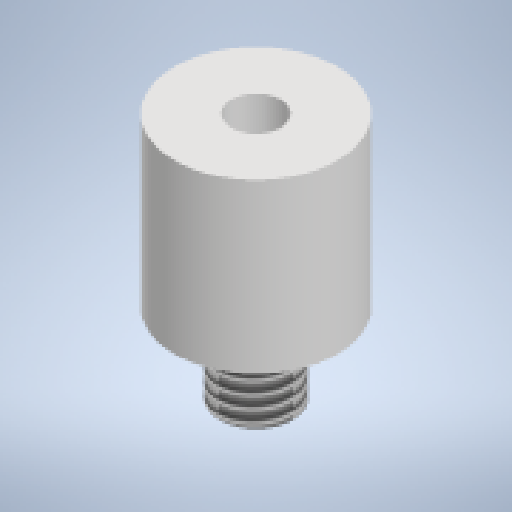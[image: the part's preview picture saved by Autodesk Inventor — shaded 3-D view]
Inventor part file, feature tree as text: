
AUTODESK INVENTOR PART (.ipt)
format: ipt  version: 2023 (Build 270158000, 158)  size: 164,864 bytes
history: native  units: mm
features: revolve x1, thread x1, sketch x1
ambient origin geometry x8: Origin, YZ Plane, XZ Plane, XY Plane, X Axis, Y Axis, Z Axis, Center Point
bodies: Solid1 (feature_tree)
feature tree (3):
  revolve  "Revolution1"  [1 undecoded]
  thread  "Thread1"  [1 undecoded]
  sketch  "Sketch1"  dims[d4=0.5mm d5=1.5mm d6=0.8mm d7=1.0mm d8=360.0deg d9=5.0mm d10=0.0mm d11=8.0mm d12=2.0mm d13=5.0mm d14=3.0mm d15=1.5mm d16=3.5mm d17=7.0mm]
note: 2 required parameter values undecoded (feature->parameter linkage not recoverable at this tier; creation-order binding heuristic only, values carry confidence <= 0.55)